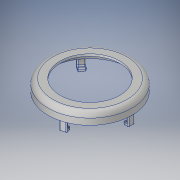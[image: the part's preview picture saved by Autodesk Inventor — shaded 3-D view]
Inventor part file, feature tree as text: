
AUTODESK INVENTOR PART (.ipt)
format: ipt  version: 2018 (Build 220112000, 112)  size: 287,232 bytes
history: native  units: in
note: dims shown in document units (in); Inventor stores cm internally (conversion verified against a paired STEP export)
features: extrude x3, sketch x3, fillet x2, shell x1, pattern_circular x1
ambient origin geometry x8: Origin, YZ Plane, XZ Plane, XY Plane, X Axis, Y Axis, Z Axis, Center Point
bodies: Solid1 (feature_tree)
feature tree (10):
  extrude  "Extrusion1"  Depth=0.0175in
  shell  "Shell1"  Thickness=0.09in
  fillet  "Fillet1"  Radius=0.0175in
  extrude  "Extrusion2"  Depth=0.075in TaperAngle=0.0deg
  extrude  "Extrusion3"  Depth=0.0075in
  fillet  "Fillet2"  Radius=1.9685in
  pattern_circular  "Circular Pattern1"  [2 undecoded]
  sketch  "Sketch1"  dims[d0=0.48in d1=0.675in d2=0.09in d3=0.0in d4=0.0175in]
  sketch  "Sketch2"  dims[d5=0.04in d6=0.075in d7=0.0in]
  sketch  "Sketch3"  dims[d8=0.0255in d9=0.0in d10=0.0075in d11=1.9685in d12=360.0deg]
note: 2 required parameter values undecoded (feature->parameter linkage not recoverable at this tier; creation-order binding heuristic only, values carry confidence <= 0.55)
